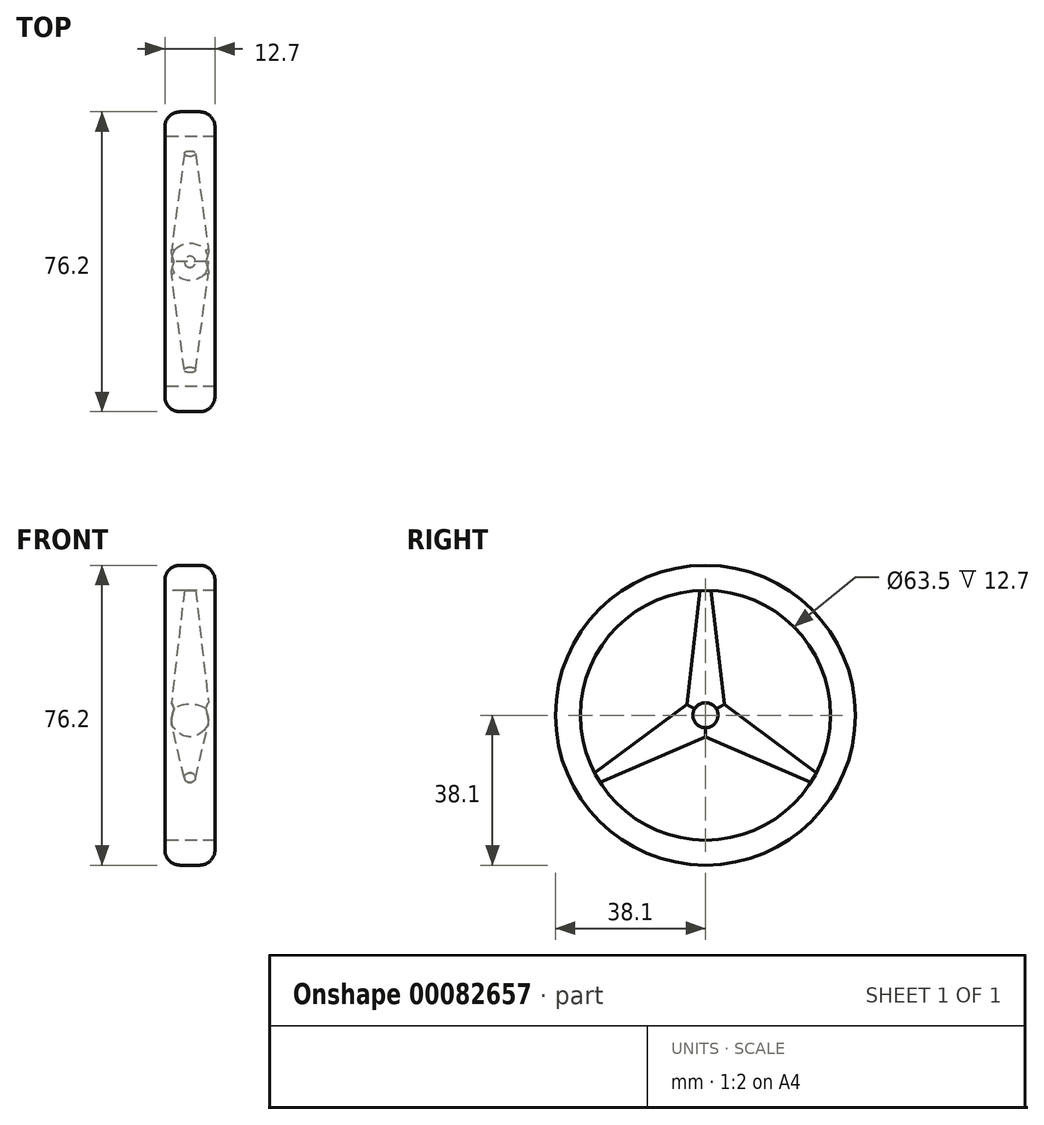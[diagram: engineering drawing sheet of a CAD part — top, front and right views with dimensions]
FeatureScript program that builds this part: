
annotation { "Feature Type Name" : "Feature", "Feature Type Description" : "" }
export const myFeature = defineFeature(function(context is Context, id is Id, definition is map)
    precondition{}
    {
        {
            var Q0;
            Q0=qCreatedBy(makeId("Right.planeOp"),FACE);
            var sketch = newSketch(context, id + "F0", { "sketchPlane" : qUnion([Q0])});
            skCircle(sketch, "E0", {"center": v(0, 0) * mm, "radius": 38.1 * mm});
            skCircle(sketch, "E1", {"center": v(0, 0) * mm, "radius": 31.75 * mm});
            skSolve(sketch);
        }
        {
            var Q0;
            Q0 = qSketchRegion(id + "F0", true);
            extrude(context, id + "F1", {"entities" : qUnion([Q0]), "depth" : 12.7 * mm});
        }
        {
            var Q0;
            Q0=makeQuery(id+"F1.opExtrude","CAP_EDGE",EDGE,{"disambiguationData":[OSD([sQuery(id+"F0.wireOp",EDGE,"E0")])],"isStart":false});
            var Q1;
            Q1=makeQuery(id+"F1.opExtrude","CAP_EDGE",EDGE,{"disambiguationData":[OSD([sQuery(id+"F0.wireOp",EDGE,"E0")])],"isStart":true});
            fillet(context, id + "F2", {"entities" : qUnion([Q0, Q1]), "radius" : 3.8 * mm, "tangentPropagation" : true, "allowEdgeOverflow" : false});
        }
        {
            var Q0;
            Q0=qCreatedBy(makeId("Top.planeOp"),FACE);
            var sketch = newSketch(context, id + "F3", { "sketchPlane" : qUnion([Q0])});
            skLineSegment(sketch, "E2", {"start": v(0, 0) * mm, "end": v(12.7, 0) * mm});
            skCircle(sketch, "E3", {"center": v(6.35, 0) * mm, "radius": 5.08 * mm});
            skSolve(sketch);
        }
        {
            var Q0;
            Q0=qCreatedBy(makeId("Top.planeOp"),FACE);
            cPlane(context, id + "F4", {"entities" : qUnion([Q0]), "cplaneType" : CPlaneType.OFFSET, "offset" : 33.02 * mm, "width" : 152.4 * mm, "height" : 152.4 * mm});
        }
        {
            var Q0;
            Q0=qCreatedBy(id+"F4.planeOp",FACE);
            var sketch = newSketch(context, id + "F5", { "sketchPlane" : qUnion([Q0])});
            skLineSegment(sketch, "E4", {"start": v(0, 0) * mm, "end": v(12.7, 0) * mm});
            skCircle(sketch, "E5", {"center": v(6.35, 0) * mm, "radius": 1.27 * mm});
            skSolve(sketch);
        }
        {
            var Q1;
            Q1 = qSketchRegion(id + "F3", true);
            var Q2;
            Q2 = qSketchRegion(id + "F5", true);
            loft(context, id + "F6", {"sheetProfilesArray" : [{ "sheetProfileEntities" : qUnion([Q1]) }, { "sheetProfileEntities" : qUnion([Q2]) }]});
        }
        {
            var Q0;
            {var subQ0=sQuery(id+"F5.wireOp",EDGE,"E5");var subQ1=sQuery(id+"F5.wireOp",EDGE,"E4");var subQ2=makeQuery(id+"F5.imprint","INTERSECT",VERTEX,{"disambiguationData":[OD(0.0)],"derivedFrom":[subQ1,subQ0]});var subQ4=makeQuery(id+"F5.imprint","IMPRINT",EDGE,{"disambiguationData":[TD([[subQ2,-1.0]])],"derivedFrom":subQ1});var subQ5=sQuery(id+"F3.wireOp",EDGE,"E3");var subQ6=sQuery(id+"F3.wireOp",EDGE,"E2");var subQ7=makeQuery(id+"F3.imprint","INTERSECT",VERTEX,{"disambiguationData":[OD(0.0)],"derivedFrom":[subQ6,subQ5]});var subQ9=makeQuery(id+"F3.imprint","IMPRINT",EDGE,{"disambiguationData":[TD([[subQ7,-1.0]])],"derivedFrom":subQ6});Q0=makeQuery(id+"F6.opLoft","SWEPT_BODY",BODY,{"disambiguationData":[OSD([makeQuery(id+"F3.imprint","IMPRINT",FACE,{"disambiguationData":[TD([[subQ9,1.0]])]}),makeQuery(id+"F3.imprint","IMPRINT",FACE,{"disambiguationData":[TD([[subQ9,-1.0]])]}),makeQuery(id+"F5.imprint","IMPRINT",FACE,{"disambiguationData":[TD([[subQ4,1.0]])]}),makeQuery(id+"F5.imprint","IMPRINT",FACE,{"disambiguationData":[TD([[subQ4,-1.0]])]})])]});}
            var Q1;
            {var subQ0=sQuery(id+"F0.wireOp",EDGE,"E0");Q1=makeQuery(id+"F2.opFillet","BLEND_EDGE",EDGE,{"blendedFrom":[makeQuery(id+"F1.opExtrude","CAP_EDGE",EDGE,{"disambiguationData":[OSD([subQ0])],"isStart":false}),makeQuery(id+"F1.opExtrude","CAP_FACE",FACE,{"disambiguationData":[OSD([subQ0,sQuery(id+"F0.wireOp",EDGE,"E1")])],"isStart":false})],"blendedInto":[makeQuery(id+"F1.opExtrude","CAP_FACE",FACE,{"disambiguationData":[OSD([subQ0,sQuery(id+"F0.wireOp",EDGE,"E1")])],"isStart":false})]});}
            circularPattern(context, id + "F7", {"operationType" : NewBodyOperationType.ADD, "entities" : qUnion([Q0]), "axis" : qUnion([Q1]), "angle" : 120 * degree, "instanceCount" : 3});
        }
        {
            var Q0;
            Q0=qCreatedBy(makeId("Right.planeOp"),FACE);
            var sketch = newSketch(context, id + "F8", { "sketchPlane" : qUnion([Q0])});
            skCircle(sketch, "E6", {"center": v(0, 0) * mm, "radius": 3.18 * mm});
            skSolve(sketch);
        }
        {
            var Q0;
            Q0 = qSketchRegion(id + "F8", true);
            extrude(context, id + "F9", {"entities" : qUnion([Q0]), "operationType" : NewBodyOperationType.REMOVE, "depth" : 25.4 * mm});
        }
    });
